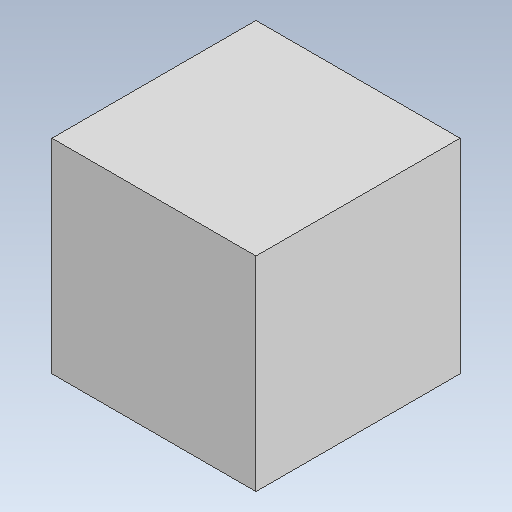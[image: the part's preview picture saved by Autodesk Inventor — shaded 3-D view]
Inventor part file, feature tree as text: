
AUTODESK INVENTOR PART (.ipt)
format: ipt  version: 2021.2 (Build 252289000, 289)  size: 88,064 bytes
history: native  units: in
note: dims shown in document units (in); Inventor stores cm internally (conversion verified against a paired STEP export)
features: extrude x1, sketch x1
ambient origin geometry x8: Origin, YZ Plane, XZ Plane, XY Plane, X Axis, Y Axis, Z Axis, Center Point
bodies: Solid1 (feature_tree)
feature tree (2):
  extrude  "Extrusion1"  Depth=1.0in
  sketch  "Sketch1"  dims[d0=1.0in d1=1.0in d2=1.0in d3=0.0in]
